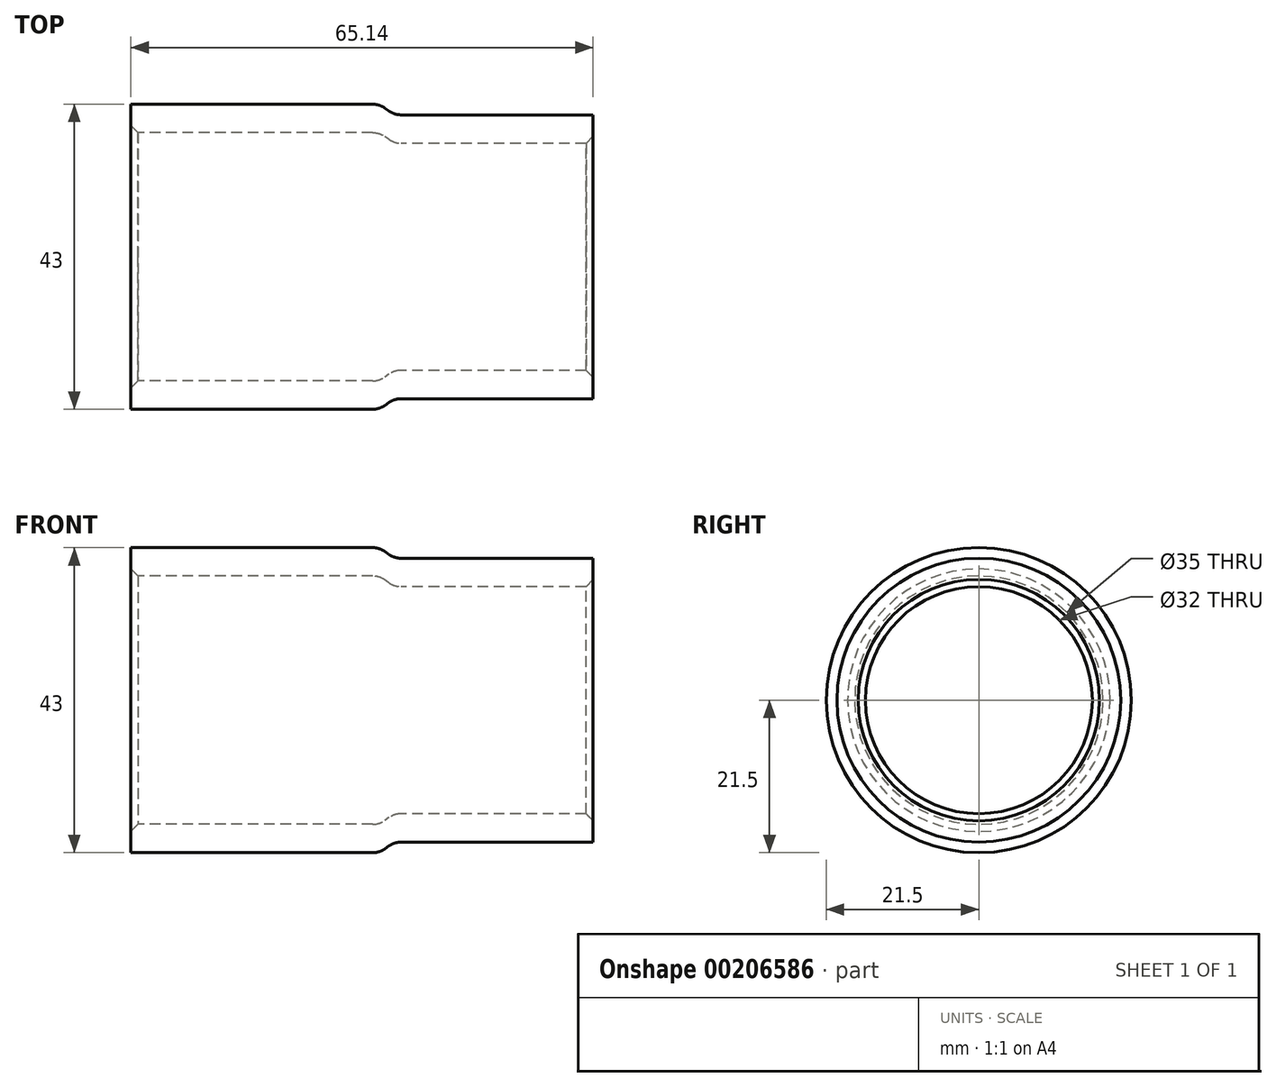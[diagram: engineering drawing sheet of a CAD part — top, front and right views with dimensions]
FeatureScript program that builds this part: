
annotation { "Feature Type Name" : "Feature", "Feature Type Description" : "" }
export const myFeature = defineFeature(function(context is Context, id is Id, definition is map)
    precondition{}
    {
        {
            var Q0;
            Q0=qCreatedBy(makeId("Front.planeOp"),FACE);
            var sketch = newSketch(context, id + "F0", { "sketchPlane" : qUnion([Q0])});
            skLineSegment(sketch, "E0", {"start": v(0, 21.5) * mm, "end": v(35, 21.5) * mm});
            skLineSegment(sketch, "E1", {"start": v(35, 21.5) * mm, "end": v(37.14, 20) * mm});
            skLineSegment(sketch, "E2", {"start": v(37.14, 20) * mm, "end": v(65.14, 20) * mm});
            skLineSegment(sketch, "E3", {"start": v(65.14, 20) * mm, "end": v(65.14, 16) * mm});
            skLineSegment(sketch, "E4", {"start": v(65.14, 16) * mm, "end": v(37.14, 16) * mm});
            skLineSegment(sketch, "E5", {"start": v(37.14, 16) * mm, "end": v(35, 17.5) * mm});
            skLineSegment(sketch, "E6", {"start": v(35, 17.5) * mm, "end": v(0, 17.5) * mm});
            skLineSegment(sketch, "E7", {"start": v(0, 17.5) * mm, "end": v(0, 21.5) * mm});
            skLineSegment(sketch, "E8", {"start": v(35, 17.5) * mm, "end": v(65.14, 17.5) * mm, "construction": true});
            skLineSegment(sketch, "E9", {"start": v(0, 0) * mm, "end": v(65.14, 0) * mm, "construction": true});
            skSolve(sketch);
        }
        {
            var Q0;
            Q0=qSketchRegion(id+"F0",true);
            var Q1;
            Q1=sQuery(id+"F0.wireOp",EDGE,"E9");
            revolve(context, id + "F1", {"entities" : qUnion([Q0]), "axis" : qUnion([Q1]), "revolveType" : RevolveType.FULL});
        }
        {
            var Q0;
            Q0=makeQuery(id+"F1.opRevolve","SWEPT_EDGE",EDGE,{"disambiguationData":[OSD([sQuery(id+"F0.wireOp",EDGE,"E6"),sQuery(id+"F0.wireOp",EDGE,"E7")])]});
            var Q1;
            Q1=makeQuery(id+"F1.opRevolve","SWEPT_EDGE",EDGE,{"disambiguationData":[OSD([sQuery(id+"F0.wireOp",EDGE,"E3"),sQuery(id+"F0.wireOp",EDGE,"E4")])]});
            chamfer(context, id + "F2", {"entities" : qUnion([Q0, Q1]), "width" : 1 * mm, "tangentPropagation" : true});
        }
        {
            var Q0;
            Q0=makeQuery(id+"F1.opRevolve","SWEPT_EDGE",EDGE,{"disambiguationData":[OSD([sQuery(id+"F0.wireOp",EDGE,"E1"),sQuery(id+"F0.wireOp",EDGE,"E2")])]});
            var Q1;
            Q1=makeQuery(id+"F1.opRevolve","SWEPT_EDGE",EDGE,{"disambiguationData":[OSD([sQuery(id+"F0.wireOp",EDGE,"E0"),sQuery(id+"F0.wireOp",EDGE,"E1")])]});
            var Q2;
            Q2=makeQuery(id+"F1.opRevolve","SWEPT_EDGE",EDGE,{"disambiguationData":[OSD([sQuery(id+"F0.wireOp",EDGE,"E4"),sQuery(id+"F0.wireOp",EDGE,"E5")])]});
            var Q3;
            Q3=makeQuery(id+"F1.opRevolve","SWEPT_EDGE",EDGE,{"disambiguationData":[OSD([sQuery(id+"F0.wireOp",EDGE,"E5"),sQuery(id+"F0.wireOp",EDGE,"E6")])]});
            fillet(context, id + "F3", {"entities" : qUnion([Q0, Q1, Q2, Q3]), "radius" : 3 * mm, "tangentPropagation" : true, "allowEdgeOverflow" : false});
        }
    });
